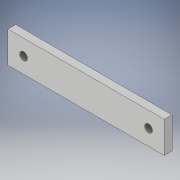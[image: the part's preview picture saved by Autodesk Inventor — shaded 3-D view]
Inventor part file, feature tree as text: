
AUTODESK INVENTOR PART (.ipt)
format: ipt  version: 2019 (Build 230136000, 136)  size: 107,008 bytes
history: native  units: in
note: dims shown in document units (in); Inventor stores cm internally (conversion verified against a paired STEP export)
features: thread x2, sketch x2, extrude x1, hole x1, plane x1, mirror x1
ambient origin geometry x8: Origin, YZ Plane, XZ Plane, XY Plane, X Axis, Y Axis, Z Axis, Center Point
bodies: Solid1 (feature_tree)
feature tree (8):
  extrude  "Extrusion1"  Depth=1.0in
  hole  "Hole1"  [1 undecoded]
  thread  "Thread1"  [1 undecoded]
  plane  "Work Plane1"
  mirror  "Mirror1"
  thread  "Thread2"  [1 undecoded]
  sketch  "Sketch1"  dims[d0=5.0in d1=1.0in]
  sketch  "Sketch2"  dims[d2=0.25in d3=0.0in d4=0.5in d5=0.25in d6=0.75in d7=0.375in d8=0.25in d9=0.5635in d10=1.0in d11=0.8108in d12=1.0in d13=0.0in d14=1.0in d15=0.0in d16=0.375in]
note: 3 required parameter values undecoded (feature->parameter linkage not recoverable at this tier; creation-order binding heuristic only, values carry confidence <= 0.55)
